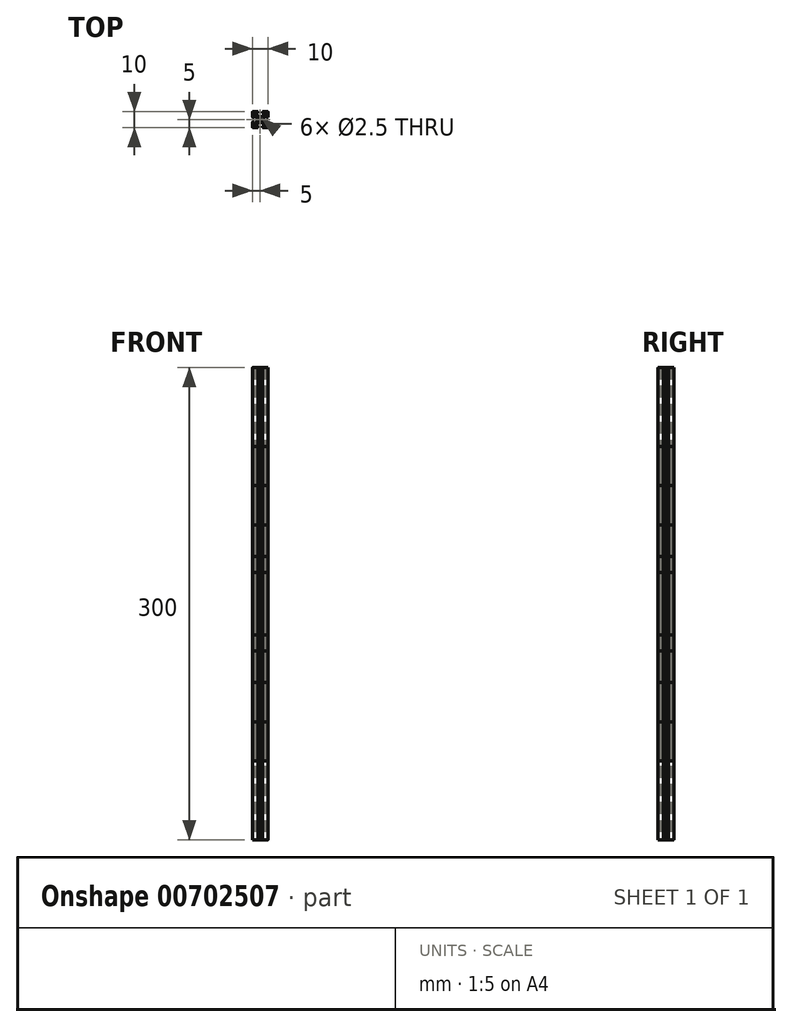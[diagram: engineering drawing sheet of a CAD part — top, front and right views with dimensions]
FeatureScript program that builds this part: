
annotation { "Feature Type Name" : "Feature", "Feature Type Description" : "" }
export const myFeature = defineFeature(function(context is Context, id is Id, definition is map)
    precondition{}
    {
        {
            var Q0;
            Q0=qCreatedBy(makeId("Top.planeOp"),FACE);
            var sketch = newSketch(context, id + "F0", { "sketchPlane" : qUnion([Q0])});
            skLineSegment(sketch, "E0", {"start": v(-2, 0) * mm, "end": v(-2, 1) * mm});
            skLineSegment(sketch, "E1", {"start": v(-2, 1) * mm, "end": v(-3.65, 2.96) * mm});
            skLineSegment(sketch, "E2", {"start": v(-4, 2.83) * mm, "end": v(-4, 1.7) * mm});
            skLineSegment(sketch, "E3", {"start": v(-4.2, 1.5) * mm, "end": v(-4.8, 1.5) * mm});
            skLineSegment(sketch, "E4", {"start": v(-5, 1.7) * mm, "end": v(-5, 4.8) * mm});
            skLineSegment(sketch, "E5", {"start": v(0, 0) * mm, "end": v(-5, 5) * mm, "construction": true});
            skArc(sketch, "E6.filletArc", {"start": v(-5, 1.7) * mm, "mid": v(-4.94, 1.56) * mm, "end": v(-4.8, 1.5) * mm});
            skPoint(sketch, "E7.visualSharp", {"position": v(-4, 1.5) * mm});
            skArc(sketch, "E7.filletArc", {"start": v(-4.2, 1.5) * mm, "mid": v(-4.06, 1.56) * mm, "end": v(-4, 1.7) * mm});
            skPoint(sketch, "E8.visualSharp", {"position": v(-4, 3.38) * mm});
            skArc(sketch, "E8.filletArc", {"start": v(-3.65, 2.96) * mm, "mid": v(-3.87, 3.02) * mm, "end": v(-4, 2.83) * mm});
            skArc(sketch, "E9", {"start": v(-5, 4.8) * mm, "mid": v(-4.98, 4.88) * mm, "end": v(-4.94, 4.94) * mm});
            skArc(sketch, "E10.MirrorCS", {"start": v(-4.8, 5) * mm, "mid": v(-4.88, 4.98) * mm, "end": v(-4.94, 4.94) * mm});
            skLineSegment(sketch, "E11.MirrorCS", {"start": v(-1.7, 5) * mm, "end": v(-4.8, 5) * mm});
            skArc(sketch, "E12.MirrorCS", {"start": v(-1.7, 5) * mm, "mid": v(-1.56, 4.94) * mm, "end": v(-1.5, 4.8) * mm});
            skLineSegment(sketch, "E13.MirrorCS", {"start": v(-1.5, 4.2) * mm, "end": v(-1.5, 4.8) * mm});
            skArc(sketch, "E14.MirrorCS", {"start": v(-1.5, 4.2) * mm, "mid": v(-1.56, 4.06) * mm, "end": v(-1.7, 4) * mm});
            skLineSegment(sketch, "E15.MirrorCS", {"start": v(-2.83, 4) * mm, "end": v(-1.7, 4) * mm});
            skArc(sketch, "E16.MirrorCS", {"start": v(-2.96, 3.65) * mm, "mid": v(-3.02, 3.87) * mm, "end": v(-2.83, 4) * mm});
            skLineSegment(sketch, "E17.MirrorCS", {"start": v(-1, 2) * mm, "end": v(-2.96, 3.65) * mm});
            skLineSegment(sketch, "E18.MirrorCS", {"start": v(0, 2) * mm, "end": v(-1, 2) * mm});
            skLineSegment(sketch, "E19.MirrorCS", {"start": v(0, 2) * mm, "end": v(1, 2) * mm});
            skLineSegment(sketch, "E20.MirrorCS", {"start": v(1, 2) * mm, "end": v(2.96, 3.65) * mm});
            skArc(sketch, "E21.MirrorCS", {"start": v(2.96, 3.65) * mm, "mid": v(3.02, 3.87) * mm, "end": v(2.83, 4) * mm});
            skLineSegment(sketch, "E22.MirrorCS", {"start": v(2.83, 4) * mm, "end": v(1.7, 4) * mm});
            skArc(sketch, "E23.MirrorCS", {"start": v(1.5, 4.2) * mm, "mid": v(1.56, 4.06) * mm, "end": v(1.7, 4) * mm});
            skLineSegment(sketch, "E24.MirrorCS", {"start": v(1.5, 4.2) * mm, "end": v(1.5, 4.8) * mm});
            skArc(sketch, "E25.MirrorCS", {"start": v(1.7, 5) * mm, "mid": v(1.56, 4.94) * mm, "end": v(1.5, 4.8) * mm});
            skLineSegment(sketch, "E26.MirrorCS", {"start": v(1.7, 5) * mm, "end": v(4.8, 5) * mm});
            skArc(sketch, "E27.MirrorCS", {"start": v(4.8, 5) * mm, "mid": v(4.88, 4.98) * mm, "end": v(4.94, 4.94) * mm});
            skArc(sketch, "E28.MirrorCS", {"start": v(5, 4.8) * mm, "mid": v(4.98, 4.88) * mm, "end": v(4.94, 4.94) * mm});
            skLineSegment(sketch, "E29.MirrorCS", {"start": v(5, 1.7) * mm, "end": v(5, 4.8) * mm});
            skArc(sketch, "E30.MirrorCS", {"start": v(5, 1.7) * mm, "mid": v(4.94, 1.56) * mm, "end": v(4.8, 1.5) * mm});
            skLineSegment(sketch, "E31.MirrorCS", {"start": v(4.2, 1.5) * mm, "end": v(4.8, 1.5) * mm});
            skArc(sketch, "E32.MirrorCS", {"start": v(4.2, 1.5) * mm, "mid": v(4.06, 1.56) * mm, "end": v(4, 1.7) * mm});
            skLineSegment(sketch, "E33.MirrorCS", {"start": v(4, 2.83) * mm, "end": v(4, 1.7) * mm});
            skArc(sketch, "E34.MirrorCS", {"start": v(3.65, 2.96) * mm, "mid": v(3.87, 3.02) * mm, "end": v(4, 2.83) * mm});
            skLineSegment(sketch, "E35.MirrorCS", {"start": v(2, 1) * mm, "end": v(3.65, 2.96) * mm});
            skLineSegment(sketch, "E36.MirrorCS", {"start": v(2, 0) * mm, "end": v(2, 1) * mm});
            skLineSegment(sketch, "E37.MirrorCS", {"start": v(-2, 0) * mm, "end": v(-2, -1) * mm});
            skLineSegment(sketch, "E38.MirrorCS", {"start": v(-2, -1) * mm, "end": v(-3.65, -2.96) * mm});
            skArc(sketch, "E39.MirrorCS", {"start": v(-3.65, -2.96) * mm, "mid": v(-3.87, -3.02) * mm, "end": v(-4, -2.83) * mm});
            skLineSegment(sketch, "E40.MirrorCS", {"start": v(-4, -2.83) * mm, "end": v(-4, -1.7) * mm});
            skArc(sketch, "E41.MirrorCS", {"start": v(-4.2, -1.5) * mm, "mid": v(-4.06, -1.56) * mm, "end": v(-4, -1.7) * mm});
            skLineSegment(sketch, "E42.MirrorCS", {"start": v(-4.2, -1.5) * mm, "end": v(-4.8, -1.5) * mm});
            skArc(sketch, "E43.MirrorCS", {"start": v(-5, -1.7) * mm, "mid": v(-4.94, -1.56) * mm, "end": v(-4.8, -1.5) * mm});
            skLineSegment(sketch, "E44.MirrorCS", {"start": v(-5, -1.7) * mm, "end": v(-5, -4.8) * mm});
            skArc(sketch, "E45.MirrorCS", {"start": v(-5, -4.8) * mm, "mid": v(-4.98, -4.88) * mm, "end": v(-4.94, -4.94) * mm});
            skArc(sketch, "E46.MirrorCS", {"start": v(-4.8, -5) * mm, "mid": v(-4.88, -4.98) * mm, "end": v(-4.94, -4.94) * mm});
            skLineSegment(sketch, "E47.MirrorCS", {"start": v(-1.7, -5) * mm, "end": v(-4.8, -5) * mm});
            skArc(sketch, "E48.MirrorCS", {"start": v(-1.7, -5) * mm, "mid": v(-1.56, -4.94) * mm, "end": v(-1.5, -4.8) * mm});
            skLineSegment(sketch, "E49.MirrorCS", {"start": v(-1.5, -4.2) * mm, "end": v(-1.5, -4.8) * mm});
            skArc(sketch, "E50.MirrorCS", {"start": v(-1.5, -4.2) * mm, "mid": v(-1.56, -4.06) * mm, "end": v(-1.7, -4) * mm});
            skLineSegment(sketch, "E51.MirrorCS", {"start": v(-2.83, -4) * mm, "end": v(-1.7, -4) * mm});
            skArc(sketch, "E52.MirrorCS", {"start": v(-2.96, -3.65) * mm, "mid": v(-3.02, -3.87) * mm, "end": v(-2.83, -4) * mm});
            skLineSegment(sketch, "E53.MirrorCS", {"start": v(-1, -2) * mm, "end": v(-2.96, -3.65) * mm});
            skLineSegment(sketch, "E54.MirrorCS", {"start": v(0, -2) * mm, "end": v(-1, -2) * mm});
            skLineSegment(sketch, "E55.MirrorCS", {"start": v(0, -2) * mm, "end": v(1, -2) * mm});
            skLineSegment(sketch, "E56.MirrorCS", {"start": v(1, -2) * mm, "end": v(2.96, -3.65) * mm});
            skArc(sketch, "E57.MirrorCS", {"start": v(2.96, -3.65) * mm, "mid": v(3.02, -3.87) * mm, "end": v(2.83, -4) * mm});
            skLineSegment(sketch, "E58.MirrorCS", {"start": v(2.83, -4) * mm, "end": v(1.7, -4) * mm});
            skArc(sketch, "E59.MirrorCS", {"start": v(1.5, -4.2) * mm, "mid": v(1.56, -4.06) * mm, "end": v(1.7, -4) * mm});
            skLineSegment(sketch, "E60.MirrorCS", {"start": v(1.5, -4.2) * mm, "end": v(1.5, -4.8) * mm});
            skArc(sketch, "E61.MirrorCS", {"start": v(1.7, -5) * mm, "mid": v(1.56, -4.94) * mm, "end": v(1.5, -4.8) * mm});
            skLineSegment(sketch, "E62.MirrorCS", {"start": v(1.7, -5) * mm, "end": v(4.8, -5) * mm});
            skArc(sketch, "E63.MirrorCS", {"start": v(4.8, -5) * mm, "mid": v(4.88, -4.98) * mm, "end": v(4.94, -4.94) * mm});
            skArc(sketch, "E64.MirrorCS", {"start": v(5, -4.8) * mm, "mid": v(4.98, -4.88) * mm, "end": v(4.94, -4.94) * mm});
            skLineSegment(sketch, "E65.MirrorCS", {"start": v(5, -1.7) * mm, "end": v(5, -4.8) * mm});
            skArc(sketch, "E66.MirrorCS", {"start": v(5, -1.7) * mm, "mid": v(4.94, -1.56) * mm, "end": v(4.8, -1.5) * mm});
            skLineSegment(sketch, "E67.MirrorCS", {"start": v(4.2, -1.5) * mm, "end": v(4.8, -1.5) * mm});
            skArc(sketch, "E68.MirrorCS", {"start": v(4.2, -1.5) * mm, "mid": v(4.06, -1.56) * mm, "end": v(4, -1.7) * mm});
            skLineSegment(sketch, "E69.MirrorCS", {"start": v(4, -2.83) * mm, "end": v(4, -1.7) * mm});
            skArc(sketch, "E70.MirrorCS", {"start": v(3.65, -2.96) * mm, "mid": v(3.87, -3.02) * mm, "end": v(4, -2.83) * mm});
            skLineSegment(sketch, "E71.MirrorCS", {"start": v(2, -1) * mm, "end": v(3.65, -2.96) * mm});
            skLineSegment(sketch, "E72.MirrorCS", {"start": v(2, 0) * mm, "end": v(2, -1) * mm});
            skCircle(sketch, "E73", {"center": v(0, 0) * mm, "radius": 1.25 * mm});
            skSolve(sketch);
        }
        {
            var Q0;
            Q0=makeQuery(id+"F0.imprint","IMPRINT",FACE,{"disambiguationData":[TD([[makeQuery(id+"F0.imprint","IMPRINT",EDGE,{"derivedFrom":sQuery(id+"F0.wireOp",EDGE,"E0")}),-1.0]])]});
            extrude(context, id + "F1", {"entities" : qUnion([Q0]), "endBound" : BoundingType.SYMMETRIC, "depth" : 40 * mm, "offsetDistance" : 25 * mm});
        }
        {
            var Q0;
            Q0=makeQuery(id+"F0.imprint","IMPRINT",FACE,{"disambiguationData":[TD([[makeQuery(id+"F0.imprint","IMPRINT",EDGE,{"derivedFrom":sQuery(id+"F0.wireOp",EDGE,"E0")}),-1.0]])]});
            extrude(context, id + "F2", {"entities" : qUnion([Q0]), "endBound" : BoundingType.SYMMETRIC, "depth" : 60 * mm, "offsetDistance" : 25 * mm});
        }
        {
            var Q0;
            Q0=makeQuery(id+"F0.imprint","IMPRINT",FACE,{"disambiguationData":[TD([[makeQuery(id+"F0.imprint","IMPRINT",EDGE,{"derivedFrom":sQuery(id+"F0.wireOp",EDGE,"E0")}),-1.0]])]});
            extrude(context, id + "F3", {"entities" : qUnion([Q0]), "endBound" : BoundingType.SYMMETRIC, "depth" : 100 * mm, "offsetDistance" : 25 * mm});
        }
        {
            var Q0;
            Q0=makeQuery(id+"F0.imprint","IMPRINT",FACE,{"disambiguationData":[TD([[makeQuery(id+"F0.imprint","IMPRINT",EDGE,{"derivedFrom":sQuery(id+"F0.wireOp",EDGE,"E0")}),-1.0]])]});
            extrude(context, id + "F4", {"entities" : qUnion([Q0]), "endBound" : BoundingType.SYMMETRIC, "depth" : 150 * mm, "offsetDistance" : 25 * mm});
        }
        {
            var Q0;
            Q0=makeQuery(id+"F0.imprint","IMPRINT",FACE,{"disambiguationData":[TD([[makeQuery(id+"F0.imprint","IMPRINT",EDGE,{"derivedFrom":sQuery(id+"F0.wireOp",EDGE,"E0")}),-1.0]])]});
            extrude(context, id + "F5", {"entities" : qUnion([Q0]), "endBound" : BoundingType.SYMMETRIC, "depth" : 200 * mm, "offsetDistance" : 25 * mm});
        }
        {
            var Q0;
            Q0=makeQuery(id+"F0.imprint","IMPRINT",FACE,{"disambiguationData":[TD([[makeQuery(id+"F0.imprint","IMPRINT",EDGE,{"derivedFrom":sQuery(id+"F0.wireOp",EDGE,"E0")}),-1.0]])]});
            extrude(context, id + "F6", {"entities" : qUnion([Q0]), "endBound" : BoundingType.SYMMETRIC, "depth" : 300 * mm, "offsetDistance" : 25 * mm});
        }
    });
